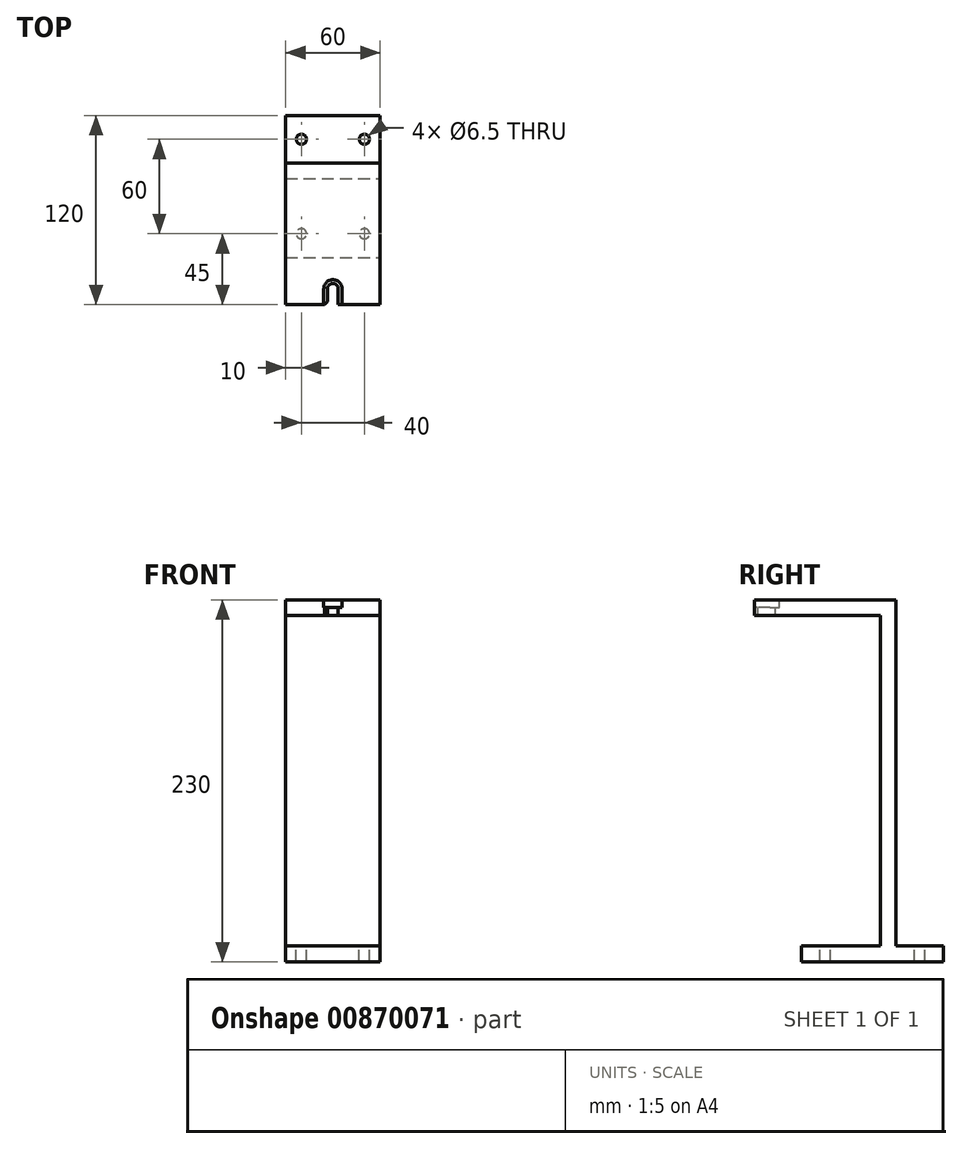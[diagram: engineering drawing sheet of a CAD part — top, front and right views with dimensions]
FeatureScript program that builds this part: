
annotation { "Feature Type Name" : "Feature", "Feature Type Description" : "" }
export const myFeature = defineFeature(function(context is Context, id is Id, definition is map)
    precondition{}
    {
        {
            var Q0;
            Q0=qCreatedBy(makeId("Front.planeOp"),FACE);
            var sketch = newSketch(context, id + "F0", { "sketchPlane" : qUnion([Q0])});
            skLineSegment(sketch, "E0.bottom", {"start": v(-30, 115) * mm, "end": v(30, 115) * mm});
            skLineSegment(sketch, "E0.top", {"start": v(-30, -115) * mm, "end": v(30, -115) * mm});
            skLineSegment(sketch, "E0.left", {"start": v(-30, 115) * mm, "end": v(-30, -115) * mm});
            skLineSegment(sketch, "E0.right", {"start": v(30, 115) * mm, "end": v(30, -115) * mm});
            skPoint(sketch, "E0.middle", {"position": v(0, 0) * mm});
            skSolve(sketch);
        }
        {
            var Q0;
            Q0 = qSketchRegion(id + "F0", true);
            extrude(context, id + "F1", {"entities" : qUnion([Q0]), "depth" : 10 * mm, "offsetDistance" : 25 * mm});
        }
        {
            var Q0;
            Q0=makeQuery(id+"F1.opExtrude","CAP_FACE",FACE,{"disambiguationData":[OSD([sQuery(id+"F0.wireOp",EDGE,"E0.bottom"),sQuery(id+"F0.wireOp",EDGE,"E0.top"),sQuery(id+"F0.wireOp",EDGE,"E0.left"),sQuery(id+"F0.wireOp",EDGE,"E0.right")])],"isStart":true});
            var sketch = newSketch(context, id + "F2", { "sketchPlane" : qUnion([Q0])});
            skLineSegment(sketch, "E1.bottom", {"start": v(-30, -115) * mm, "end": v(30, -115) * mm});
            skLineSegment(sketch, "E1.top", {"start": v(-30, -105) * mm, "end": v(30, -105) * mm});
            skLineSegment(sketch, "E1.left", {"start": v(-30, -115) * mm, "end": v(-30, -105) * mm});
            skLineSegment(sketch, "E1.right", {"start": v(30, -115) * mm, "end": v(30, -105) * mm});
            skSolve(sketch);
        }
        {
            var Q0;
            Q0 = qSketchRegion(id + "F2", true);
            extrude(context, id + "F3", {"entities" : qUnion([Q0]), "operationType" : NewBodyOperationType.ADD, "depth" : 30 * mm, "offsetDistance" : 25 * mm});
        }
        {
            var Q0;
            Q0=makeQuery(id+"F3.opExtrude","SWEPT_FACE",FACE,{"disambiguationData":[OSD([sQuery(id+"F2.wireOp",EDGE,"E1.top")])]});
            var sketch = newSketch(context, id + "F4", { "sketchPlane" : qUnion([Q0])});
            skCircle(sketch, "E2", {"center": v(20, 15) * mm, "radius": 3.25 * mm});
            skCircle(sketch, "E3", {"center": v(-20, 15) * mm, "radius": 3.25 * mm});
            skSolve(sketch);
        }
        {
            var Q0;
            Q0 = qSketchRegion(id + "F4", true);
            extrude(context, id + "F5", {"entities" : qUnion([Q0]), "operationType" : NewBodyOperationType.REMOVE, "endBound" : BoundingType.THROUGH_ALL, "oppositeDirection" : true, "depth" : 25 * mm, "offsetDistance" : 25 * mm});
        }
        {
            var Q0;
            Q0=makeQuery(id+"F1.opExtrude","CAP_FACE",FACE,{"disambiguationData":[OSD([sQuery(id+"F0.wireOp",EDGE,"E0.bottom"),sQuery(id+"F0.wireOp",EDGE,"E0.top"),sQuery(id+"F0.wireOp",EDGE,"E0.left"),sQuery(id+"F0.wireOp",EDGE,"E0.right")])],"isStart":false});
            var sketch = newSketch(context, id + "F6", { "sketchPlane" : qUnion([Q0])});
            skLineSegment(sketch, "E4.bottom", {"start": v(-30, 115) * mm, "end": v(30, 115) * mm});
            skLineSegment(sketch, "E4.top", {"start": v(-30, 105) * mm, "end": v(30, 105) * mm});
            skLineSegment(sketch, "E4.left", {"start": v(-30, 115) * mm, "end": v(-30, 105) * mm});
            skLineSegment(sketch, "E4.right", {"start": v(30, 115) * mm, "end": v(30, 105) * mm});
            skSolve(sketch);
        }
        {
            var Q0;
            Q0 = qSketchRegion(id + "F6", true);
            extrude(context, id + "F7", {"entities" : qUnion([Q0]), "operationType" : NewBodyOperationType.ADD, "depth" : 80 * mm, "offsetDistance" : 25 * mm});
        }
        {
            var Q0;
            Q0=makeQuery(id+"F1.opExtrude","CAP_FACE",FACE,{"disambiguationData":[OSD([sQuery(id+"F0.wireOp",EDGE,"E0.bottom"),sQuery(id+"F0.wireOp",EDGE,"E0.top"),sQuery(id+"F0.wireOp",EDGE,"E0.left"),sQuery(id+"F0.wireOp",EDGE,"E0.right")])],"isStart":false});
            var sketch = newSketch(context, id + "F8", { "sketchPlane" : qUnion([Q0])});
            skLineSegment(sketch, "E5.bottom", {"start": v(-30, -115) * mm, "end": v(30, -115) * mm});
            skLineSegment(sketch, "E5.top", {"start": v(-30, -105) * mm, "end": v(30, -105) * mm});
            skLineSegment(sketch, "E5.left", {"start": v(-30, -115) * mm, "end": v(-30, -105) * mm});
            skLineSegment(sketch, "E5.right", {"start": v(30, -115) * mm, "end": v(30, -105) * mm});
            skSolve(sketch);
        }
        {
            var Q0;
            Q0 = qSketchRegion(id + "F8", true);
            extrude(context, id + "F9", {"entities" : qUnion([Q0]), "operationType" : NewBodyOperationType.ADD, "depth" : 50 * mm, "offsetDistance" : 25 * mm});
        }
        {
            var Q0;
            Q0=makeQuery(id+"F9.opExtrude","SWEPT_FACE",FACE,{"disambiguationData":[OSD([sQuery(id+"F8.wireOp",EDGE,"E5.top")])]});
            var sketch = newSketch(context, id + "F10", { "sketchPlane" : qUnion([Q0])});
            skCircle(sketch, "E6", {"center": v(20, -45) * mm, "radius": 3.25 * mm});
            skCircle(sketch, "E7", {"center": v(-20, -45) * mm, "radius": 3.25 * mm});
            skSolve(sketch);
        }
        {
            var Q0;
            Q0 = qSketchRegion(id + "F10", true);
            extrude(context, id + "F11", {"entities" : qUnion([Q0]), "operationType" : NewBodyOperationType.REMOVE, "endBound" : BoundingType.THROUGH_ALL, "oppositeDirection" : true, "depth" : 25 * mm, "offsetDistance" : 25 * mm});
        }
        {
            var Q0;
            Q0=makeQuery(id+"F7.boolean.opBoolean","MERGE",FACE,{"derivedFrom":[makeQuery(id+"F1.opExtrude","SWEPT_FACE",FACE,{"disambiguationData":[OSD([sQuery(id+"F0.wireOp",EDGE,"E0.bottom")])]}),makeQuery(id+"F7.opExtrude","SWEPT_FACE",FACE,{"disambiguationData":[OSD([sQuery(id+"F6.wireOp",EDGE,"E4.bottom")])]})]});
            var sketch = newSketch(context, id + "F12", { "sketchPlane" : qUnion([Q0])});
            skArc(sketch, "E8", {"start": v(3.4, -80) * mm, "mid": v(0, -76.6) * mm, "end": v(-3.4, -80) * mm});
            skLineSegment(sketch, "E9", {"start": v(0, -90) * mm, "end": v(3.4, -90) * mm});
            skLineSegment(sketch, "E10", {"start": v(3.4, -90) * mm, "end": v(3.4, -80) * mm});
            skLineSegment(sketch, "E11", {"start": v(0, -90) * mm, "end": v(-3.4, -90) * mm});
            skLineSegment(sketch, "E12", {"start": v(-3.4, -90) * mm, "end": v(-3.4, -80) * mm});
            skSolve(sketch);
        }
        {
            var Q0;
            Q0 = qSketchRegion(id + "F12", true);
            extrude(context, id + "F13", {"entities" : qUnion([Q0]), "operationType" : NewBodyOperationType.REMOVE, "endBound" : BoundingType.THROUGH_ALL, "oppositeDirection" : true, "depth" : 25 * mm, "offsetDistance" : 25 * mm});
        }
        {
            var Q0;
            Q0=makeQuery(id+"F7.boolean.opBoolean","MERGE",FACE,{"derivedFrom":[makeQuery(id+"F1.opExtrude","SWEPT_FACE",FACE,{"disambiguationData":[OSD([sQuery(id+"F0.wireOp",EDGE,"E0.bottom")])]}),makeQuery(id+"F7.opExtrude","SWEPT_FACE",FACE,{"disambiguationData":[OSD([sQuery(id+"F6.wireOp",EDGE,"E4.bottom")])]})]});
            var sketch = newSketch(context, id + "F14", { "sketchPlane" : qUnion([Q0])});
            skArc(sketch, "E13", {"start": v(5.8, -80) * mm, "mid": v(0, -74.2) * mm, "end": v(-5.8, -80) * mm});
            skLineSegment(sketch, "E14", {"start": v(5.8, -90) * mm, "end": v(5.8, -80) * mm});
            skLineSegment(sketch, "E15.MirrorCS", {"start": v(-5.8, -90) * mm, "end": v(-5.8, -80) * mm});
            skArc(sketch, "E16.0", {"start": v(3.4, -80) * mm, "mid": v(0, -76.6) * mm, "end": v(-3.4, -80) * mm});
            skLineSegment(sketch, "E17", {"start": v(5.8, -90) * mm, "end": v(-5.8, -90) * mm});
            skSolve(sketch);
        }
        {
            var Q0;
            Q0 = qSketchRegion(id + "F14", true);
            extrude(context, id + "F15", {"entities" : qUnion([Q0]), "operationType" : NewBodyOperationType.REMOVE, "oppositeDirection" : true, "depth" : 5 * mm, "offsetDistance" : 25 * mm});
        }
        {
            var Q0;
            Q0=makeQuery(id+"F13.boolean.opBoolean","COPY",EDGE,{"derivedFrom":makeQuery(id+"F13.opExtrude","SWEPT_EDGE",EDGE,{"disambiguationData":[OSD([sQuery(id+"F6.wireOp",EDGE,"E4.bottom"),sQuery(id+"F12.wireOp",EDGE,"E9"),sQuery(id+"F12.wireOp",EDGE,"E10")])]})});
            var Q1;
            Q1=makeQuery(id+"F13.boolean.opBoolean","COPY",EDGE,{"derivedFrom":makeQuery(id+"F13.opExtrude","SWEPT_EDGE",EDGE,{"disambiguationData":[OSD([sQuery(id+"F6.wireOp",EDGE,"E4.bottom"),sQuery(id+"F12.wireOp",EDGE,"E11"),sQuery(id+"F12.wireOp",EDGE,"E12")])]})});
            var Q2;
            Q2=makeQuery(id+"F15.boolean.opBoolean","COPY",EDGE,{"derivedFrom":makeQuery(id+"F15.opExtrude","SWEPT_EDGE",EDGE,{"disambiguationData":[OSD([sQuery(id+"F6.wireOp",EDGE,"E4.bottom"),sQuery(id+"F14.wireOp",EDGE,"E14"),sQuery(id+"F14.wireOp",EDGE,"E17")])]})});
            var Q3;
            Q3=makeQuery(id+"F15.boolean.opBoolean","COPY",EDGE,{"derivedFrom":makeQuery(id+"F15.opExtrude","SWEPT_EDGE",EDGE,{"disambiguationData":[OSD([sQuery(id+"F6.wireOp",EDGE,"E4.bottom"),sQuery(id+"F14.wireOp",EDGE,"E15.MirrorCS"),sQuery(id+"F14.wireOp",EDGE,"E17")])]})});
            chamfer(context, id + "F16", {"entities" : qUnion([Q0, Q1, Q2, Q3]), "width" : 2 * mm, "tangentPropagation" : true});
        }
    });
